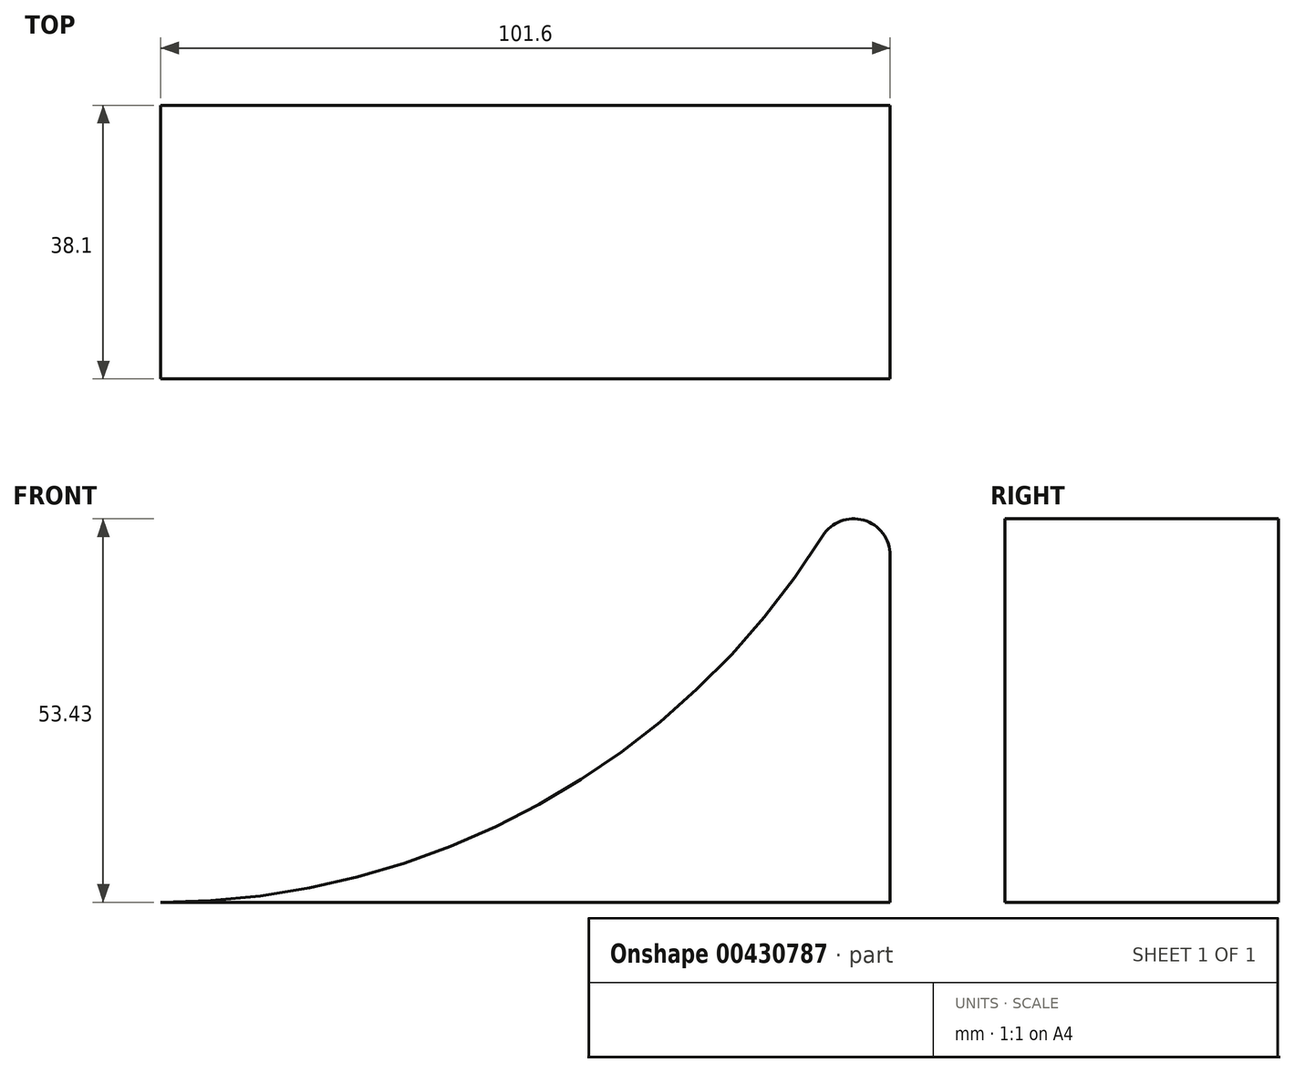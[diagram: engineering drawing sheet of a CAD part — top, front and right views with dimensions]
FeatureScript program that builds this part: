
annotation { "Feature Type Name" : "Feature", "Feature Type Description" : "" }
export const myFeature = defineFeature(function(context is Context, id is Id, definition is map)
    precondition{}
    {
        {
            var Q0;
            Q0=qCreatedBy(makeId("Front.planeOp"),FACE);
            var sketch = newSketch(context, id + "F0", { "sketchPlane" : qUnion([Q0])});
            skLineSegment(sketch, "E0", {"start": v(0, 0) * mm, "end": v(304.8, 0) * mm});
            skLineSegment(sketch, "E1", {"start": v(304.8, 0) * mm, "end": v(304.8, 69.85) * mm});
            skLineSegment(sketch, "E2", {"start": v(304.8, 0) * mm, "end": v(203.2, 0) * mm});
            skArc(sketch, "E3", {"start": v(203.2, 0) * mm, "mid": v(264.85, 19.15) * mm, "end": v(304.8, 69.85) * mm});
            skLineSegment(sketch, "E4", {"start": v(0, 0) * mm, "end": v(0, 25.4) * mm});
            skLineSegment(sketch, "E5", {"start": v(0, 25.4) * mm, "end": v(171.45, 25.4) * mm});
            skLineSegment(sketch, "E6", {"start": v(171.45, 25.4) * mm, "end": v(189.18, 73) * mm});
            skLineSegment(sketch, "E7", {"start": v(189.18, 73) * mm, "end": v(201.08, 68.57) * mm});
            skLineSegment(sketch, "E8", {"start": v(201.08, 68.57) * mm, "end": v(187.78, 32.87) * mm});
            skArc(sketch, "E9", {"start": v(187.78, 32.87) * mm, "mid": v(252.3, 32.37) * mm, "end": v(304.8, 69.85) * mm});
            skSolve(sketch);
        }
        {
            var Q0;
            Q0=makeQuery(id+"F0.imprint","IMPRINT",FACE,{"disambiguationData":[TD([[makeQuery(id+"F0.imprint","IMPRINT",EDGE,{"derivedFrom":sQuery(id+"F0.wireOp",EDGE,"E0")}),1.0]])]});
            extrude(context, id + "F1", {"entities" : qUnion([Q0]), "depth" : 38.1 * mm});
        }
        {
            var Q0;
            Q0=makeQuery(id+"F1.opExtrude","CAP_FACE",FACE,{"disambiguationData":[OSD([sQuery(id+"F0.wireOp",EDGE,"E0"),sQuery(id+"F0.wireOp",EDGE,"E3"),sQuery(id+"F0.wireOp",EDGE,"E4"),sQuery(id+"F0.wireOp",EDGE,"E5"),sQuery(id+"F0.wireOp",EDGE,"E6"),sQuery(id+"F0.wireOp",EDGE,"E7"),sQuery(id+"F0.wireOp",EDGE,"E8"),sQuery(id+"F0.wireOp",EDGE,"E9")])],"isStart":false});
            var sketch = newSketch(context, id + "F2", { "sketchPlane" : qUnion([Q0])});
            skLineSegment(sketch, "E10", {"start": v(0, 0) * mm, "end": v(10.16, 0) * mm});
            skLineSegment(sketch, "E11", {"start": v(10.16, 0) * mm, "end": v(10.16, 12.7) * mm});
            skPoint(sketch, "E11.endSnap0", {"position": v(0, 12.7) * mm});
            skCircle(sketch, "E12", {"center": v(10.16, 12.7) * mm, "radius": 3.81 * mm});
            skSolve(sketch);
        }
        {
            var Q0;
            Q0=makeQuery(id+"F2.imprint","IMPRINT",FACE,{"disambiguationData":[TD([[makeQuery(id+"F2.imprint","IMPRINT",EDGE,{"derivedFrom":sQuery(id+"F2.wireOp",EDGE,"E12")}),1.0]])]});
            extrude(context, id + "F3", {"entities" : qUnion([Q0]), "operationType" : NewBodyOperationType.REMOVE, "oppositeDirection" : true, "depth" : 50.8 * mm});
        }
        {
            var Q0;
            Q0=makeQuery(id+"F1.opExtrude","SWEPT_EDGE",EDGE,{"disambiguationData":[OSD([sQuery(id+"F0.wireOp",EDGE,"E8"),sQuery(id+"F0.wireOp",EDGE,"E9")])]});
            fillet(context, id + "F4", {"entities" : qUnion([Q0]), "radius" : 5.08 * mm, "tangentPropagation" : true, "allowEdgeOverflow" : false});
        }
    });
